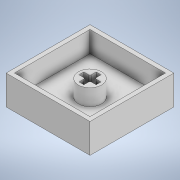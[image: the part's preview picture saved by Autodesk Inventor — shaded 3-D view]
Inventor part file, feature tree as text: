
AUTODESK INVENTOR PART (.ipt)
format: ipt  version: 2021.1 (Build 251245000, 245)  size: 135,680 bytes
history: native  units: mm
features: extrude x3, sketch x3, fillet x1
ambient origin geometry x8: Origin, YZ Plane, XZ Plane, XY Plane, X Axis, Y Axis, Z Axis, Center Point
bodies: Solid1 (feature_tree)
feature tree (7):
  extrude  "Extrusion1"  Depth=5.0mm TaperAngle=0.0deg
  extrude  "Extrusion2"  Depth=0.3mm
  extrude  "Extrusion4"  [1 undecoded]
  fillet  "Fillet1"  [1 undecoded]
  sketch  "Sketch1"  dims[d0=2.0mm d1=0.0mm d2=5.0mm d3=0.0mm]
  sketch  "Sketch2"  dims[d11=3.9mm d12=0.0mm d13=0.3mm]
  sketch  "Sketch3"
note: 2 required parameter values undecoded (feature->parameter linkage not recoverable at this tier; creation-order binding heuristic only, values carry confidence <= 0.55)
